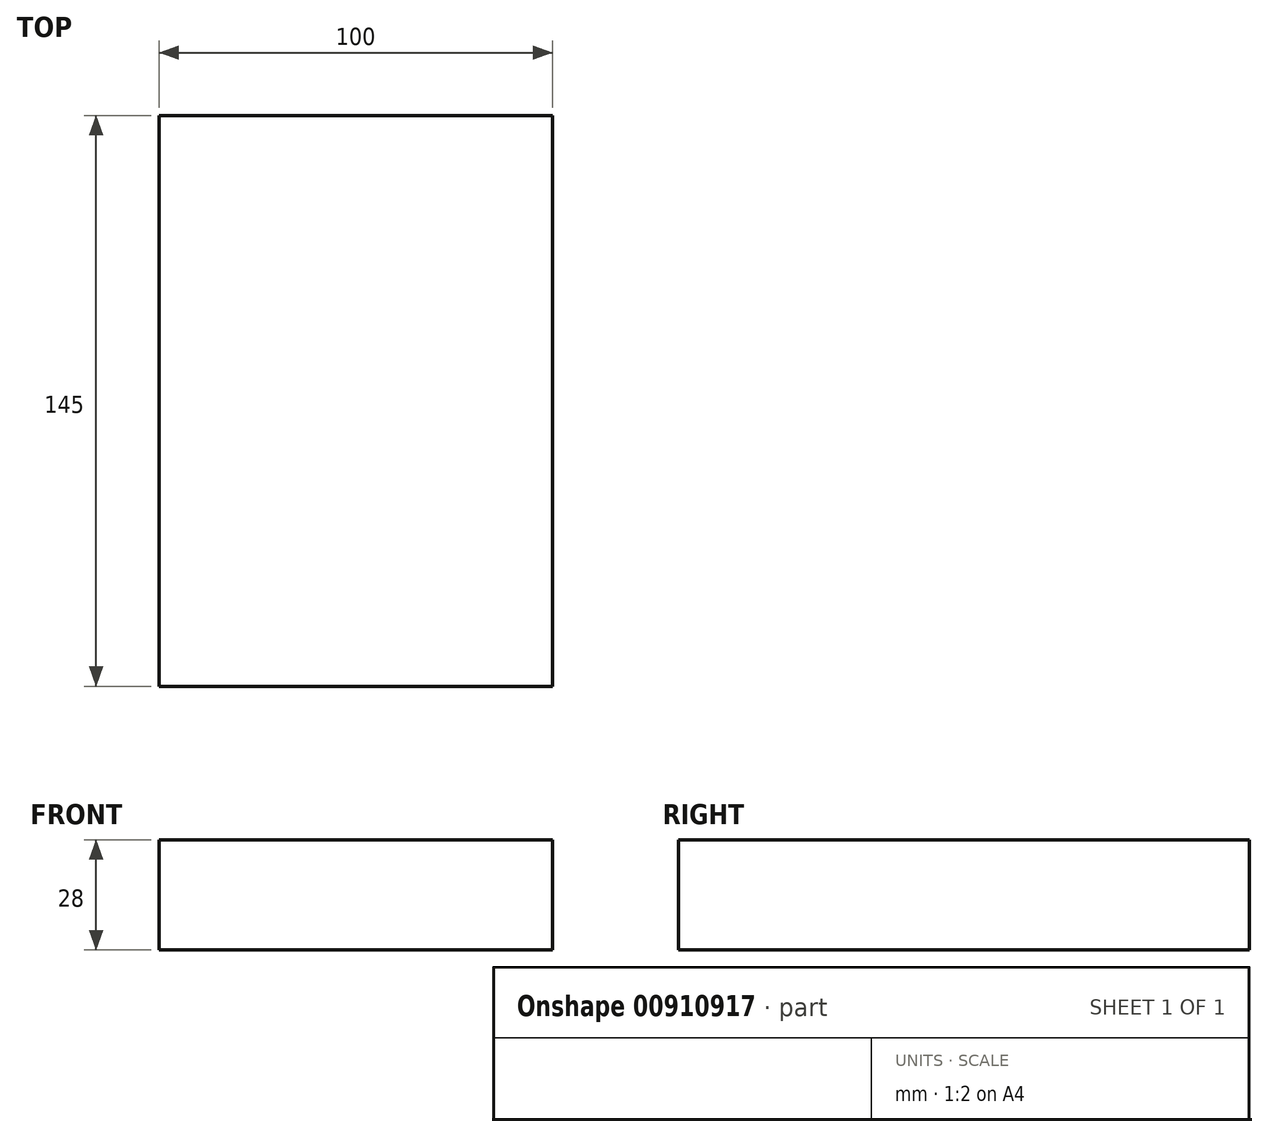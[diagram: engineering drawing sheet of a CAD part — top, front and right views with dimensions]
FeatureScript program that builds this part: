
annotation { "Feature Type Name" : "Feature", "Feature Type Description" : "" }
export const myFeature = defineFeature(function(context is Context, id is Id, definition is map)
    precondition{}
    {
        {
            var Q0;
            Q0=qCreatedBy(makeId("Top.planeOp"),FACE);
            var sketch = newSketch(context, id + "F0", { "sketchPlane" : qUnion([Q0])});
            skLineSegment(sketch, "E0.bottom", {"start": v(-52.44, -71.12) * mm, "end": v(-52.44, 73.88) * mm});
            skLineSegment(sketch, "E0.top", {"start": v(47.56, -71.12) * mm, "end": v(47.56, 73.88) * mm});
            skLineSegment(sketch, "E0.left", {"start": v(-52.44, -71.12) * mm, "end": v(47.56, -71.12) * mm});
            skLineSegment(sketch, "E0.right", {"start": v(-52.44, 73.88) * mm, "end": v(47.56, 73.88) * mm});
            skSolve(sketch);
        }
        {
            var Q0;
            Q0 = qSketchRegion(id + "F0", true);
            extrude(context, id + "F1", {"entities" : qUnion([Q0]), "depth" : 28 * mm, "offsetDistance" : 25 * mm});
        }
    });
